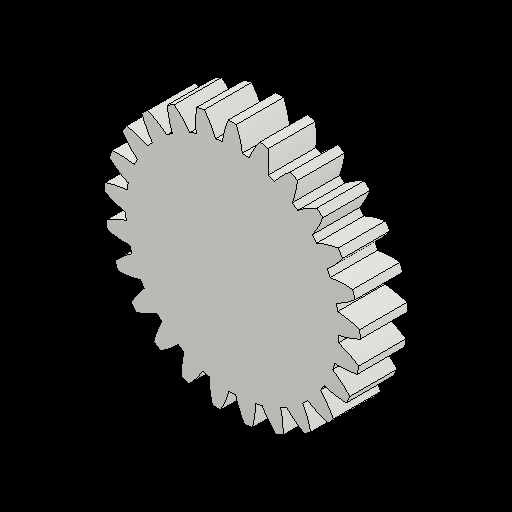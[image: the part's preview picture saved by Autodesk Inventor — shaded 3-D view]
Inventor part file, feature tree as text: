
AUTODESK INVENTOR PART (.ipt)
format: ipt  version: 2023.2 (Build 272271030, 271C)  size: 225,280 bytes
history: native  units: mm (DEFAULTED — no unit token found)
features: plane x3, other x3, sketch x2, extrude x1
ambient origin geometry x8: Origin, YZ Plane, XZ Plane, XY Plane, X Axis, Y Axis, Z Axis, Center Point
bodies: Solid1 (feature_tree)
feature tree (9):
  extrude  "Extrusion1"  Depth=5.0mm TaperAngle=0.0deg
  plane  "Work Plane2"
  plane  "Work Plane8"
  plane  "Work Plane9"
  other  "Spur Gear"
  sketch  "Sketch1"  dims[d0=27.0mm d1=5.0mm d2=0.0mm]
  sketch  "Sketch2"  dims[d3=25.0mm d4=10.0mm d5=0.0mm d16=16.5mm d17=0.0mm d34=1.256637mm d39=0.0mm d41=0.0mm d43=16.5mm d46=16.5mm d47=0.0mm d48=0.0mm]
  other  "Srf1"
  other  "Pitch Diameter"
